# Revit family: Faucet-Lavatory-KOHLER-ACCLIV-K-33064T_1
name_source: partatom
category: Plumbing Fixtures
units: mm (PartAtom-declared; Revit-internal decimal feet)

## family parameters
Cut with Voids When Loaded = No
Host = Face
OmniClass Number = 23.31.11.00
OmniClass Title = Faucets
Part Type = Normal
Room Calculation Point = No
Round Connector Dimension = Use Diameter
Shared = No

## types (7) — shared parameters
ADA Compliant = No
Assembly Code = D2010
CW Connection = Yes
Cold Water Inlet = Cold Water Inlet
Date Modified = 11/23/2022
Default Elevation = 36"
Faucet Hole Spacing = 0"
Flow Rate = 2 GPM
HW Connection = Yes
Handle Clearance = 4 1/16"
Height = 12 3/16"
Hot Water Inlet = Hot Water Inlet
Length = 5 11/16"
Manufacturer = Kohler Co.
Master Format 2014 = 22 41 39
Master Format 2014 Name = Residential Faucets, Supplies, and Trim
Material = Premium Metal Construction
Product Name = ACCLIV
Spout Reach = 5 11/16"
URL = http://www.kohler.com.cn
Vent Connection = No
Waste Connection = No
Waste Water Outlet = Waste Water Outlet
WaterSense Certified = No
Width = 2"

## per-type parameters (varying)
| type | Description | Drain Included | Finish | Model | Pressure | Product Documentation Link | Product Page URL | Type |
| 2.2 GPM, With Drain, AF-Vibrant French Gold | Keling single bowl faucet (high spout) | Yes | Kohler-Metal-AF-Vibrant_French_Gold | K-33064T-4-AF | 60.00 psi | https://files.kohler.com.cn | https://www.kohler.com.cn | 1 |
| 2.2 GPM, With Drain, BL-Matte Black | Keling single bowl faucet (high spout) | Yes | Kohler-Metal-BL-Matte_Black | K-33064T-4-BL | 60.00 psi | https://files.kohler.com.cn |  | 2 |
| 2.2 GPM, With Drain, BN-Vibrant Brushed Nickel | Keling single bowl faucet (high spout) | Yes | Kohler-Metal-BN-Vibrant_Brushed_Nickel | K-33064T-4-BN | 60.00 psi | https://files.kohler.com.cn | https://www.kohler.com.cn | 3 |
| 2.2 GPM, With Drain, CP-Polished Chrome | Keling single bowl faucet (high spout) | Yes | Kohler-Metal-CP-Polished_Chrome | K-33064T-4-CP | 60.00 psi | https://files.kohler.com.cn | https://www.kohler.com.cn | 4 |
| 1.85 GPM, Without Drain, AF-Vibrant French Gold | Super Tall Lavatory Faucet -Paddle Handle | No | Kohler-Metal-AF-Vibrant_French_Gold | K-33064T-4ND-AF | 45.00 psi |  |  | 5 |
| 1.85 GPM, Without Drain, BN-Vibrant Brushed Nickel | Super Tall Lavatory Faucet -Paddle Handle | No | Kohler-Metal-BN-Vibrant_Brushed_Nickel | K-33064T-4ND-BN | 45.00 psi |  |  | 6 |
| 1.85 GPM, Without Drain, CP-Polished Chrome | Super Tall Lavatory Faucet -Paddle Handle | No | Kohler-Metal-CP-Polished_Chrome | K-33064T-4ND-CP | 45.00 psi |  |  | 7 |

## geometry (parser evidence)
native form markers: Sweep x6
no freeform markers — native parametric forms only
